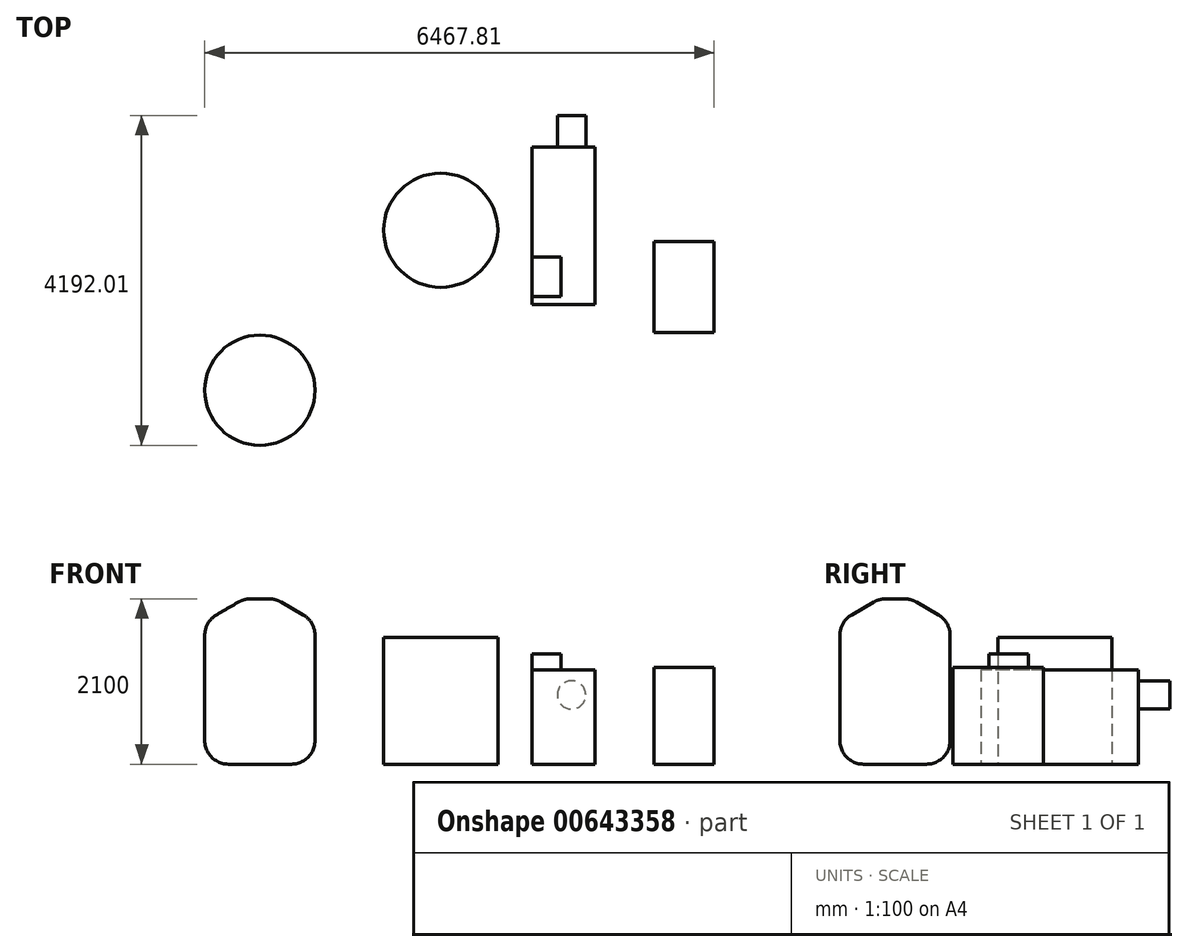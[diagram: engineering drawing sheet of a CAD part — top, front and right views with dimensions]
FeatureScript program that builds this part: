
annotation { "Feature Type Name" : "Feature", "Feature Type Description" : "" }
export const myFeature = defineFeature(function(context is Context, id is Id, definition is map)
    precondition{}
    {
        {
            var Q0;
            Q0=qCreatedBy(makeId("Top.planeOp"),FACE);
            var sketch = newSketch(context, id + "F0", { "sketchPlane" : qUnion([Q0])});
            skLineSegment(sketch, "E0.bottom", {"start": v(-411.47, -694.24) * mm, "end": v(348.53, -694.24) * mm});
            skLineSegment(sketch, "E0.top", {"start": v(-411.47, 455.76) * mm, "end": v(348.53, 455.76) * mm});
            skLineSegment(sketch, "E0.left", {"start": v(-411.47, -694.24) * mm, "end": v(-411.47, 455.76) * mm});
            skLineSegment(sketch, "E0.right", {"start": v(348.53, -694.24) * mm, "end": v(348.53, 455.76) * mm});
            skSolve(sketch);
        }
        {
            var Q0;
            Q0=qSketchRegion(id+"F0",true);
            extrude(context, id + "F1", {"entities" : qUnion([Q0]), "depth" : 1230 * mm, "offsetDistance" : 25 * mm});
        }
        {
            var Q0;
            Q0=qCreatedBy(makeId("Top.planeOp"),FACE);
            var sketch = newSketch(context, id + "F2", { "sketchPlane" : qUnion([Q0])});
            skCircle(sketch, "E1", {"center": v(-3121.8, 602.2) * mm, "radius": 725 * mm});
            skSolve(sketch);
        }
        {
            var Q0;
            Q0=makeQuery(id+"F2.imprint","IMPRINT",FACE,{"disambiguationData":[TD([[makeQuery(id+"F2.imprint","IMPRINT",EDGE,{"derivedFrom":sQuery(id+"F2.wireOp",EDGE,"E1")}),1.0]])]});
            extrude(context, id + "F3", {"entities" : qUnion([Q0]), "depth" : 1610 * mm, "offsetDistance" : 25 * mm});
        }
        {
            var Q0;
            Q0=qCreatedBy(makeId("Top.planeOp"),FACE);
            var sketch = newSketch(context, id + "F4", { "sketchPlane" : qUnion([Q0])});
            skLineSegment(sketch, "E2.bottom", {"start": v(-1964.82, 1661.78) * mm, "end": v(-1164.82, 1661.78) * mm});
            skLineSegment(sketch, "E2.top", {"start": v(-1964.82, -338.22) * mm, "end": v(-1164.82, -338.22) * mm});
            skLineSegment(sketch, "E2.left", {"start": v(-1964.82, 1661.78) * mm, "end": v(-1964.82, -338.22) * mm});
            skLineSegment(sketch, "E2.right", {"start": v(-1164.82, 1661.78) * mm, "end": v(-1164.82, -338.22) * mm});
            skSolve(sketch);
        }
        {
            var Q0;
            Q0=qSketchRegion(id+"F4",true);
            extrude(context, id + "F5", {"entities" : qUnion([Q0]), "depth" : 1200 * mm, "offsetDistance" : 25 * mm});
        }
        {
            var Q0;
            Q0=makeQuery(id+"F5.opExtrude","CAP_FACE",FACE,{"disambiguationData":[OSD([sQuery(id+"F4.wireOp",EDGE,"E2.bottom"),sQuery(id+"F4.wireOp",EDGE,"E2.top"),sQuery(id+"F4.wireOp",EDGE,"E2.left"),sQuery(id+"F4.wireOp",EDGE,"E2.right")])],"isStart":false});
            var sketch = newSketch(context, id + "F6", { "sketchPlane" : qUnion([Q0])});
            skLineSegment(sketch, "E3.bottom", {"start": v(-1594.82, 261.78) * mm, "end": v(-1964.82, 261.78) * mm});
            skLineSegment(sketch, "E3.top", {"start": v(-1594.82, -238.22) * mm, "end": v(-1964.82, -238.22) * mm});
            skLineSegment(sketch, "E3.left", {"start": v(-1594.82, 261.78) * mm, "end": v(-1594.82, -238.22) * mm});
            skLineSegment(sketch, "E3.right", {"start": v(-1964.82, 261.78) * mm, "end": v(-1964.82, -238.22) * mm});
            skSolve(sketch);
        }
        {
            var Q0;
            Q0=qSketchRegion(id+"F6",true);
            extrude(context, id + "F7", {"entities" : qUnion([Q0]), "operationType" : NewBodyOperationType.ADD, "depth" : 200 * mm, "offsetDistance" : 25 * mm});
        }
        {
            var Q0;
            Q0=qCreatedBy(makeId("Top.planeOp"),FACE);
            var sketch = newSketch(context, id + "F8", { "sketchPlane" : qUnion([Q0])});
            skCircle(sketch, "E4", {"center": v(-5419.28, -1430.23) * mm, "radius": 700 * mm});
            skSolve(sketch);
        }
        {
            var Q0;
            Q0=qSketchRegion(id+"F8",true);
            extrude(context, id + "F9", {"entities" : qUnion([Q0]), "depth" : 2100 * mm, "offsetDistance" : 25 * mm});
        }
        {
            var Q0;
            Q0=makeQuery(id+"F9.opExtrude","CAP_EDGE",EDGE,{"disambiguationData":[OSD([sQuery(id+"F8.wireOp",EDGE,"E4")])],"isStart":true});
            fillet(context, id + "F10", {"entities" : qUnion([Q0]), "radius" : 300 * mm, "tangentPropagation" : true, "allowEdgeOverflow" : false});
        }
        {
            var Q0;
            Q0=makeQuery(id+"F9.opExtrude","CAP_EDGE",EDGE,{"disambiguationData":[OSD([sQuery(id+"F8.wireOp",EDGE,"E4")])],"isStart":false});
            chamfer(context, id + "F11", {"entities" : qUnion([Q0]), "chamferType" : ChamferType.OFFSET_ANGLE, "width" : 500 * mm, "oppositeDirection" : false, "angle" : 30 * degree, "tangentPropagation" : true});
        }
        {
            var Q0;
            {var subQ0=sQuery(id+"F8.wireOp",EDGE,"E4");Q0=makeQuery(id+"F11.opChamfer","BLEND_EDGE",EDGE,{"blendedFrom":[makeQuery(id+"F9.opExtrude","CAP_EDGE",EDGE,{"disambiguationData":[OSD([subQ0])],"isStart":false}),makeQuery(id+"F9.opExtrude","SWEPT_FACE",FACE,{"disambiguationData":[OSD([subQ0])]})],"blendedInto":[makeQuery(id+"F9.opExtrude","SWEPT_FACE",FACE,{"disambiguationData":[OSD([subQ0])]})]});}
            var Q1;
            {var subQ0=sQuery(id+"F8.wireOp",EDGE,"E4");Q1=makeQuery(id+"F11.opChamfer","BLEND_EDGE",EDGE,{"blendedFrom":[makeQuery(id+"F9.opExtrude","CAP_EDGE",EDGE,{"disambiguationData":[OSD([subQ0])],"isStart":false}),makeQuery(id+"F9.opExtrude","CAP_FACE",FACE,{"disambiguationData":[OSD([subQ0])],"isStart":false})],"blendedInto":[makeQuery(id+"F9.opExtrude","CAP_FACE",FACE,{"disambiguationData":[OSD([subQ0])],"isStart":false})]});}
            fillet(context, id + "F12", {"entities" : qUnion([Q0, Q1]), "radius" : 300 * mm, "tangentPropagation" : true, "allowEdgeOverflow" : false});
        }
        {
            var Q0;
            Q0=makeQuery(id+"F5.opExtrude","SWEPT_FACE",FACE,{"disambiguationData":[OSD([sQuery(id+"F4.wireOp",EDGE,"E2.bottom")])]});
            var sketch = newSketch(context, id + "F13", { "sketchPlane" : qUnion([Q0])});
            skCircle(sketch, "E5", {"center": v(1460.07, 879.37) * mm, "radius": 180.7 * mm});
            skSolve(sketch);
        }
        {
            var Q0;
            Q0 = qSketchRegion(id + "F13", true);
            extrude(context, id + "F14", {"entities" : qUnion([Q0]), "operationType" : NewBodyOperationType.ADD, "depth" : 400 * mm, "offsetDistance" : 25 * mm});
        }
    });
